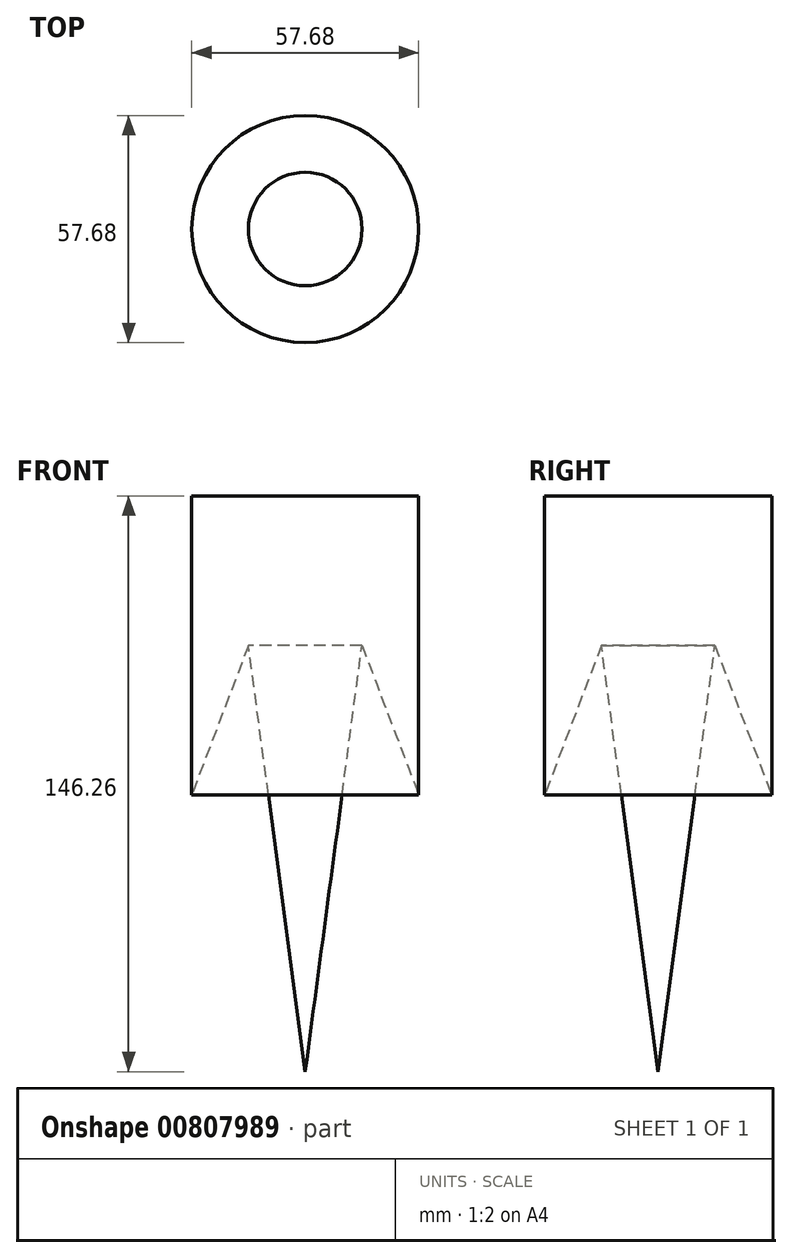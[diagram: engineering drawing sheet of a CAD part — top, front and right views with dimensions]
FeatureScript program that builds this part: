
annotation { "Feature Type Name" : "Feature", "Feature Type Description" : "" }
export const myFeature = defineFeature(function(context is Context, id is Id, definition is map)
    precondition{}
    {
        {
            var Q0;
            Q0=qCreatedBy(makeId("Front.planeOp"),FACE);
            var sketch = newSketch(context, id + "F0", { "sketchPlane" : qUnion([Q0])});
            skLineSegment(sketch, "E0", {"start": v(0, 75.93) * mm, "end": v(28.84, 75.93) * mm});
            skLineSegment(sketch, "E1", {"start": v(28.84, 75.93) * mm, "end": v(28.84, 0) * mm});
            skLineSegment(sketch, "E2", {"start": v(28.84, 0) * mm, "end": v(14.42, 37.96) * mm});
            skPoint(sketch, "E2.endSnap0", {"position": v(14.42, 75.93) * mm});
            skPoint(sketch, "E2.endSnap1", {"position": v(28.84, 37.96) * mm});
            skLineSegment(sketch, "E3", {"start": v(14.42, 37.96) * mm, "end": v(0, -70.33) * mm});
            skLineSegment(sketch, "E4", {"start": v(0, -70.33) * mm, "end": v(0, 75.93) * mm});
            skSolve(sketch);
        }
        {
            var Q0;
            Q0=sQuery(id+"F0.wireOp",EDGE,"E3");
            var Q1;
            Q1=sQuery(id+"F0.wireOp",EDGE,"E2");
            var Q2;
            Q2=sQuery(id+"F0.wireOp",EDGE,"E1");
            var Q3;
            Q3=sQuery(id+"F0.wireOp",EDGE,"E4");
            revolve(context, id + "F1", {"bodyType" : ToolBodyType.SURFACE, "surfaceOperationType" : NewSurfaceOperationType.NEW, "surfaceEntities" : qUnion([Q0, Q1, Q2]), "axis" : qUnion([Q3]), "revolveType" : RevolveType.FULL});
        }
    });
